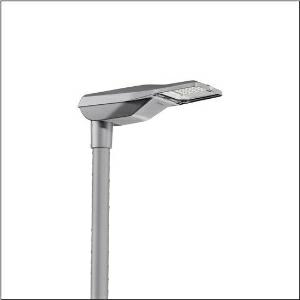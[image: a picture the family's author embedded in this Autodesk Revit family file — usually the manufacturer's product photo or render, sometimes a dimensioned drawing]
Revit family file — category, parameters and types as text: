
# Revit family: streetlight_sl_21_iq_micro___p0_5a_5xe1v31g08cb_6456
name_source: partatom
category: Lighting Fixtures
units: mm (PartAtom-declared; Revit-internal decimal feet)

## family parameters
Cut with Voids When Loaded = No
Host = Face
Light Source = No
Part Type = Normal
Room Calculation Point = No
Round Connector Dimension = Use Diameter
Shared = No

## types (1)
- --- (1 x LED, 2780 lm, 19.4 W, 3000K)
    Apparent Load = 19 VA
    CIE Flux Codes = 37 73 96 100 100
    Color Rendering = 70
    Color Temperature = 3000K
    Default Elevation = 1800 mm
    Description = Streetlight SL 21 iQ micro, mast luminaire, primary light control with lens, of PMMA, primary optical cover: cover, of toughened safety glass, transparent, light distribution: P0.5a, light emission: direct distribution, primary light characteristic: asymmetric, installation type: post-top, side-entry, LED, High Power LED, rated luminous flux: 2.780lm, luminous efficacy: 143lm/W, light colour: 730, colour temperature: 3000K, control gear: iQ Street-Remote, control: pre-setting: linear dimming characteristic, Street-Remote, Auto-Match, Temp-Guard, Lumen-Switch, Night-Set, Smart-Wire, Light-Fading, Desk-Remote (wireless, voltage-free reading and setting of iQ features in the workshop via application-optimized NFC function/RFID function), optimised constant luminous flux control (CLO 2.0), mains connection: 220..240V, AC, 50/60Hz, start of lifetime: 19W, end of service life: 20W, reduction: 10W, luminaire housing, of diecast aluminium, powder-coated, Siteco® metallic grey (DB 702S), corrosivity category C5 mid according to DIN EN ISO 12944, please order mast flange separately, inclination adjustable: 0°, 5°, 10°, 15°, sealing non-destructively replaceable, multi-level sealing system, length: 528mm, width: 235mm, height: 110mm, mast flange for spigot size: 42mm (side-entry): 5XC10008XM4, 60/48mm (side-entry/post-top): 5XC10108XM2, 76/60mm (side-entry/post-top): 5XC10108XM1, protection rating (complete): IP66, insulation class (complete): insulation class II (safety insulation), certification: CE, ENEC, ENEC+, VDE, impact resistance: IK10, permissible operating ambient temperature for outdoor applications: -40..+50°C, standard-compliant lighting for roads and squares, packaging unit: 1 piece

Light Distribution: P0.5a
    Height = 110 mm
    Lamp = 1 x LED
    Lamp Light Flux = 2780 lm
    Lamp Power = 19.4 W
    Lamp count = 1
    Length = 528 mm
    Luminous efficacy = 143 lm/W
    Manufacturer = Siteco
    ModVariant = No
    Model = 5XE1V31G08CB
    Number of Poles = 1
    OnlyDefault = Yes
    Power Factor = 1
    Product Name = Streetlight SL 21 iQ micro | P0.5a
    Product group = mast luminaire | pylon top
    ProductGroupID = 6100
    Protection Class = Protection class II
    Protection Degree = IP 66
    RLX_Detail_Level = 1
    RLX_Emergency_Light_Flux = 0 lm
    RLX_Emergency_Type = 0
    RLX_Emergency_Type_DB = No
    RlxData = <blob elided: 99041 chars, md5=e9b2d6f0>
    Socket = socket
    Standby Power = 0 W
    System Light Flux = 2780 lm
    System Power = 19 W
    Type Comments = factory setting: luminous flux: 100 % | dim-lin: 254 | 387 mA
    Type Image = l_1006881.jpg
    URL = http://relux.com
    VarID = @adj_070294
    Voltage = 0 V
    Weight = 0.00 kg
    Width = 235 mm

## geometry (parser evidence)
native form markers: Blend x4, Sweep x11
no freeform markers — native parametric forms only
